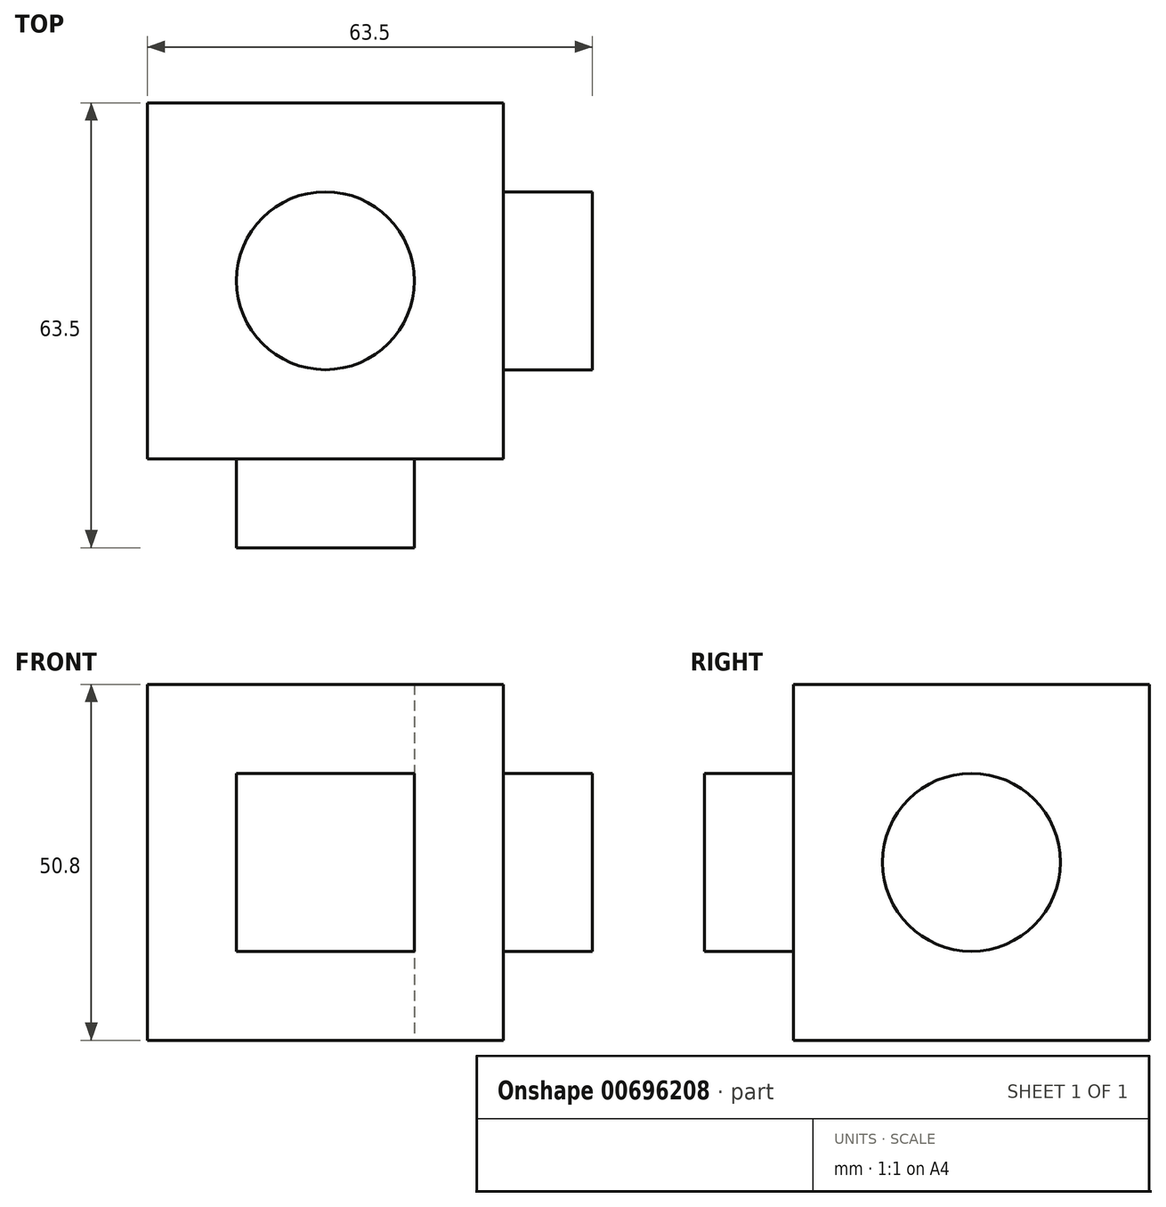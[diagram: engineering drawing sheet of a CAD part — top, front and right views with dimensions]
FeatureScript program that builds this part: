
annotation { "Feature Type Name" : "Feature", "Feature Type Description" : "" }
export const myFeature = defineFeature(function(context is Context, id is Id, definition is map)
    precondition{}
    {
        {
            var Q0;
            Q0=qCreatedBy(makeId("Top.planeOp"),FACE);
            var sketch = newSketch(context, id + "F0", { "sketchPlane" : qUnion([Q0])});
            skLineSegment(sketch, "E0.bottom", {"start": v(0, 0) * mm, "end": v(50.8, 0) * mm});
            skLineSegment(sketch, "E0.top", {"start": v(0, 50.8) * mm, "end": v(50.8, 50.8) * mm});
            skLineSegment(sketch, "E0.left", {"start": v(0, 0) * mm, "end": v(0, 50.8) * mm});
            skLineSegment(sketch, "E0.right", {"start": v(50.8, 0) * mm, "end": v(50.8, 50.8) * mm});
            skCircle(sketch, "E1", {"center": v(25.4, 25.4) * mm, "radius": 12.7 * mm});
            skSolve(sketch);
        }
        {
            var Q0;
            Q0=makeQuery(id+"F0.imprint","IMPRINT",FACE,{"disambiguationData":[TD([[makeQuery(id+"F0.imprint","IMPRINT",EDGE,{"derivedFrom":sQuery(id+"F0.wireOp",EDGE,"E0.bottom")}),1.0]])]});
            extrude(context, id + "F1", {"entities" : qUnion([Q0]), "depth" : 50.8 * mm, "offsetDistance" : 25.4 * mm});
        }
        {
            var Q0;
            Q0=makeQuery(id+"F1.opExtrude","SWEPT_FACE",FACE,{"disambiguationData":[OSD([sQuery(id+"F0.wireOp",EDGE,"E0.right")])]});
            var sketch = newSketch(context, id + "F2", { "sketchPlane" : qUnion([Q0])});
            skCircle(sketch, "E2", {"center": v(25.4, 25.4) * mm, "radius": 12.7 * mm});
            skSolve(sketch);
        }
        {
            var Q0;
            Q0=makeQuery(id+"F2.imprint","IMPRINT",FACE,{"disambiguationData":[TD([[makeQuery(id+"F2.imprint","IMPRINT",EDGE,{"derivedFrom":sQuery(id+"F2.wireOp",EDGE,"E2")}),1.0]])]});
            extrude(context, id + "F3", {"entities" : qUnion([Q0]), "operationType" : NewBodyOperationType.ADD, "depth" : 12.7 * mm, "offsetDistance" : 25.4 * mm});
        }
        {
            var Q0;
            Q0=makeQuery(id+"F1.opExtrude","SWEPT_FACE",FACE,{"disambiguationData":[OSD([sQuery(id+"F0.wireOp",EDGE,"E0.bottom")])]});
            var sketch = newSketch(context, id + "F4", { "sketchPlane" : qUnion([Q0])});
            skLineSegment(sketch, "E3.bottom", {"start": v(12.7, 12.7) * mm, "end": v(38.1, 12.7) * mm});
            skLineSegment(sketch, "E3.top", {"start": v(12.7, 38.1) * mm, "end": v(38.1, 38.1) * mm});
            skLineSegment(sketch, "E3.left", {"start": v(12.7, 12.7) * mm, "end": v(12.7, 38.1) * mm});
            skLineSegment(sketch, "E3.right", {"start": v(38.1, 12.7) * mm, "end": v(38.1, 38.1) * mm});
            skSolve(sketch);
        }
        {
            var Q0;
            Q0=makeQuery(id+"F4.imprint","IMPRINT",FACE,{"disambiguationData":[TD([[makeQuery(id+"F4.imprint","IMPRINT",EDGE,{"derivedFrom":sQuery(id+"F4.wireOp",EDGE,"E3.bottom")}),1.0]])]});
            extrude(context, id + "F5", {"entities" : qUnion([Q0]), "operationType" : NewBodyOperationType.ADD, "depth" : 12.7 * mm, "offsetDistance" : 25.4 * mm});
        }
    });
